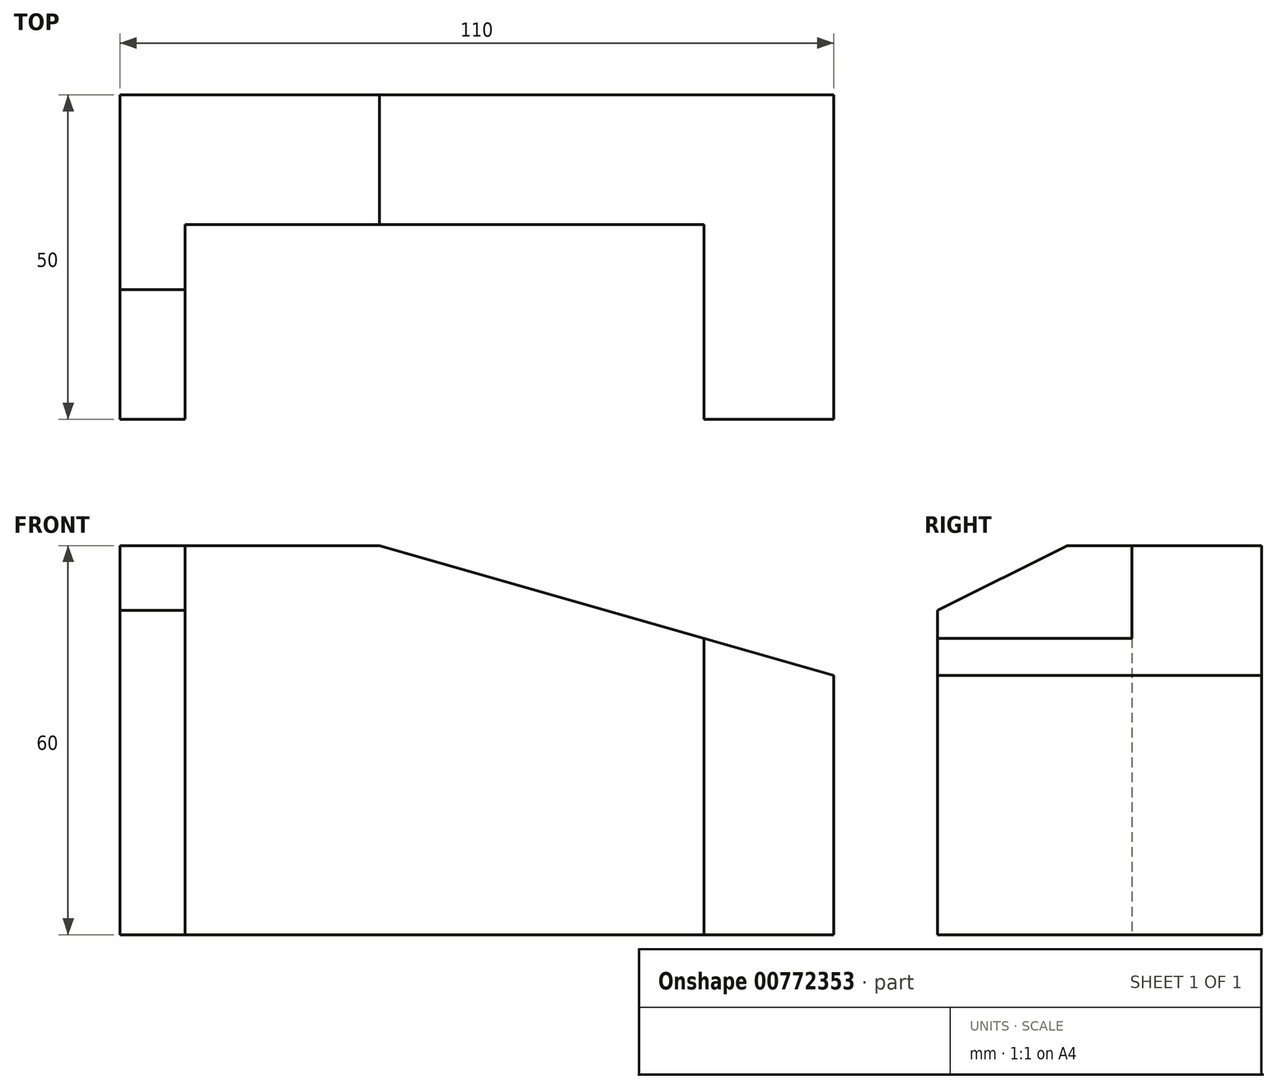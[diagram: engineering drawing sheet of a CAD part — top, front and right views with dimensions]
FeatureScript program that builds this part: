
annotation { "Feature Type Name" : "Feature", "Feature Type Description" : "" }
export const myFeature = defineFeature(function(context is Context, id is Id, definition is map)
    precondition{}
    {
        {
            var Q0;
            Q0=qCreatedBy(makeId("Top.planeOp"),FACE);
            var sketch = newSketch(context, id + "F0", { "sketchPlane" : qUnion([Q0])});
            skLineSegment(sketch, "E0", {"start": v(0, 0) * mm, "end": v(110, 0) * mm});
            skLineSegment(sketch, "E1", {"start": v(110, 0) * mm, "end": v(110, -50) * mm});
            skLineSegment(sketch, "E2", {"start": v(110, -50) * mm, "end": v(90, -50) * mm});
            skLineSegment(sketch, "E3", {"start": v(90, -50) * mm, "end": v(90, -20) * mm});
            skLineSegment(sketch, "E4", {"start": v(90, -20) * mm, "end": v(10, -20) * mm});
            skLineSegment(sketch, "E5", {"start": v(10, -20) * mm, "end": v(10, -50) * mm});
            skLineSegment(sketch, "E6", {"start": v(10, -50) * mm, "end": v(0, -50) * mm});
            skLineSegment(sketch, "E7", {"start": v(0, -50) * mm, "end": v(0, 0) * mm});
            skLineSegment(sketch, "E8", {"start": v(0, -30) * mm, "end": v(10, -30) * mm});
            skLineSegment(sketch, "E9", {"start": v(40, 0) * mm, "end": v(40, -20) * mm});
            skSolve(sketch);
        }
        {
            var Q0;
            Q0 = qSketchRegion(id + "F0", true);
            extrude(context, id + "F1", {"entities" : qUnion([Q0]), "depth" : 60 * mm, "offsetDistance" : 25 * mm});
        }
        {
            var Q0;
            Q0=makeQuery(id+"F1.opExtrude","CAP_EDGE",EDGE,{"disambiguationData":[OSD([sQuery(id+"F0.wireOp",EDGE,"E1")])],"isStart":false});
            chamfer(context, id + "F2", {"entities" : qUnion([Q0]), "chamferType" : ChamferType.TWO_OFFSETS, "width1" : 70 * mm, "oppositeDirection" : true, "width2" : 20 * mm, "tangentPropagation" : true});
        }
        {
            var Q0;
            Q0=makeQuery(id+"F1.opExtrude","CAP_EDGE",EDGE,{"disambiguationData":[OSD([sQuery(id+"F0.wireOp",EDGE,"E6")])],"isStart":false});
            chamfer(context, id + "F3", {"entities" : qUnion([Q0]), "chamferType" : ChamferType.TWO_OFFSETS, "width1" : 10 * mm, "oppositeDirection" : false, "width2" : 20 * mm, "tangentPropagation" : true});
        }
    });
